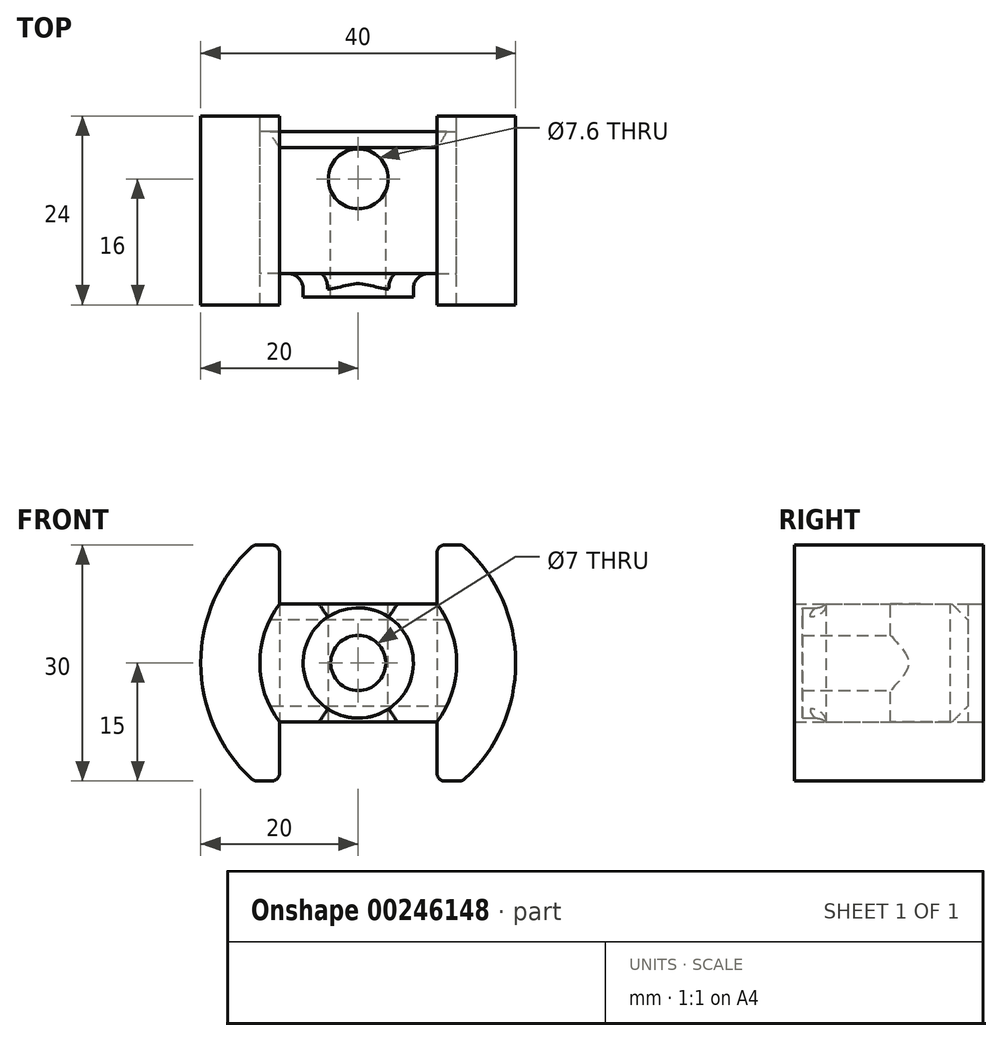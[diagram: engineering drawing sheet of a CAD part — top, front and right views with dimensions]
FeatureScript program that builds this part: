
annotation { "Feature Type Name" : "Feature", "Feature Type Description" : "" }
export const myFeature = defineFeature(function(context is Context, id is Id, definition is map)
    precondition{}
    {
        {
            var Q0;
            Q0=qCreatedBy(makeId("Front.planeOp"),FACE);
            var sketch = newSketch(context, id + "F0", { "sketchPlane" : qUnion([Q0])});
            skArc(sketch, "E0", {"start": v(-13.23, 15) * mm, "mid": v(-20, 0) * mm, "end": v(-13.23, -15) * mm});
            skArc(sketch, "E1", {"start": v(-10, 7.5) * mm, "mid": v(-12.5, 0) * mm, "end": v(-10, -7.5) * mm});
            skLineSegment(sketch, "E2.bottom", {"start": v(-13.23, 15) * mm, "end": v(-10, 15) * mm});
            skLineSegment(sketch, "E2.top", {"start": v(-13.23, -15) * mm, "end": v(-10, -15) * mm});
            skArc(sketch, "E3.trimOffspring", {"start": v(13.23, -15) * mm, "mid": v(20, 0) * mm, "end": v(13.23, 15) * mm});
            skLineSegment(sketch, "E4.bottom", {"start": v(10, 7.5) * mm, "end": v(-10, 7.5) * mm});
            skLineSegment(sketch, "E4.top", {"start": v(10, -7.5) * mm, "end": v(-10, -7.5) * mm});
            skLineSegment(sketch, "E4.left", {"start": v(10, 7.5) * mm, "end": v(10, -7.5) * mm});
            skLineSegment(sketch, "E4.right", {"start": v(-10, 7.5) * mm, "end": v(-10, -7.5) * mm});
            skLineSegment(sketch, "E5", {"start": v(-10, 7.5) * mm, "end": v(-10, 15) * mm});
            skLineSegment(sketch, "E6", {"start": v(10, 7.5) * mm, "end": v(10, 15) * mm});
            skLineSegment(sketch, "E7", {"start": v(10, -7.5) * mm, "end": v(10, -15) * mm});
            skLineSegment(sketch, "E8", {"start": v(-10, -7.5) * mm, "end": v(-10, -15) * mm});
            skLineSegment(sketch, "E9.trimOffspring", {"start": v(10, -15) * mm, "end": v(13.23, -15) * mm});
            skLineSegment(sketch, "E10.trimOffspring", {"start": v(10, 15) * mm, "end": v(13.23, 15) * mm});
            skArc(sketch, "E11.trimOffspring", {"start": v(10, -7.5) * mm, "mid": v(12.5, 0) * mm, "end": v(10, 7.5) * mm});
            skCircle(sketch, "E12", {"center": v(0, 0) * mm, "radius": 7 * mm});
            skCircle(sketch, "E13", {"center": v(0, 0) * mm, "radius": 3.5 * mm});
            skSolve(sketch);
        }
        {
            var Q0;
            Q0=makeQuery(id+"F0.imprint","IMPRINT",FACE,{"disambiguationData":[TD([[makeQuery(id+"F0.imprint","IMPRINT",EDGE,{"derivedFrom":sQuery(id+"F0.wireOp",EDGE,"E0")}),1.0]])]});
            var Q1;
            Q1=makeQuery(id+"F0.imprint","IMPRINT",FACE,{"disambiguationData":[TD([[makeQuery(id+"F0.imprint","IMPRINT",EDGE,{"derivedFrom":sQuery(id+"F0.wireOp",EDGE,"E3.trimOffspring")}),1.0]])]});
            extrude(context, id + "F1", {"entities" : qUnion([Q0, Q1]), "depth" : 24 * mm});
        }
        {
            var Q0;
            Q0=makeQuery(id+"F0.imprint","IMPRINT",FACE,{"disambiguationData":[TD([[makeQuery(id+"F0.imprint","IMPRINT",EDGE,{"derivedFrom":sQuery(id+"F0.wireOp",EDGE,"E1")}),1.0]])]});
            var Q1;
            Q1=makeQuery(id+"F0.imprint","IMPRINT",FACE,{"disambiguationData":[TD([[makeQuery(id+"F0.imprint","IMPRINT",EDGE,{"derivedFrom":sQuery(id+"F0.wireOp",EDGE,"E12")}),1.0]])]});
            var Q2;
            Q2=makeQuery(id+"F0.imprint","IMPRINT",FACE,{"disambiguationData":[TD([[makeQuery(id+"F0.imprint","IMPRINT",EDGE,{"derivedFrom":sQuery(id+"F0.wireOp",EDGE,"E4.bottom")}),1.0]])]});
            var Q3;
            Q3=makeQuery(id+"F0.imprint","IMPRINT",FACE,{"disambiguationData":[TD([[makeQuery(id+"F0.imprint","IMPRINT",EDGE,{"derivedFrom":sQuery(id+"F0.wireOp",EDGE,"E4.left")}),1.0]])]});
            extrude(context, id + "F2", {"entities" : qUnion([Q0, Q1, Q2, Q3]), "depth" : 20 * mm, "hasSecondDirection" : true, "secondDirectionOppositeDirection" : false, "secondDirectionDepth" : 2 * mm});
        }
        {
            var Q0;
            Q0=makeQuery(id+"F0.imprint","IMPRINT",FACE,{"disambiguationData":[TD([[makeQuery(id+"F0.imprint","IMPRINT",EDGE,{"derivedFrom":sQuery(id+"F0.wireOp",EDGE,"E12")}),1.0]])]});
            var Q1;
            Q1=makeQuery(id+"F0.imprint","IMPRINT",FACE,{"disambiguationData":[TD([[makeQuery(id+"F0.imprint","IMPRINT",EDGE,{"derivedFrom":sQuery(id+"F0.wireOp",EDGE,"E13")}),1.0]])]});
            extrude(context, id + "F3", {"entities" : qUnion([Q0, Q1]), "operationType" : NewBodyOperationType.ADD, "depth" : 23 * mm, "hasSecondDirection" : true, "secondDirectionOppositeDirection" : false, "secondDirectionDepth" : 2 * mm});
        }
        {
            var Q0;
            Q0=makeQuery(id+"F2.opExtrude","SWEPT_FACE",FACE,{"disambiguationData":[OSD([sQuery(id+"F0.wireOp",EDGE,"E4.top")])]});
            var sketch = newSketch(context, id + "F4", { "sketchPlane" : qUnion([Q0])});
            skLineSegment(sketch, "E14", {"start": v(0, 0) * mm, "end": v(0, 8) * mm});
            skCircle(sketch, "E15", {"center": v(0, 8) * mm, "radius": 3.8 * mm});
            skSolve(sketch);
        }
        {
            var Q0;
            Q0=sQuery(id+"F4.wireOp",VERTEX,"E15.center");
            var Q1;
            Q1=makeQuery(id+"F2.opExtrude","SWEPT_BODY",BODY,{"disambiguationData":[OSD([sQuery(id+"F0.wireOp",EDGE,"E1"),sQuery(id+"F0.wireOp",EDGE,"E4.bottom"),sQuery(id+"F0.wireOp",EDGE,"E4.top"),sQuery(id+"F0.wireOp",EDGE,"E11.trimOffspring"),sQuery(id+"F0.wireOp",EDGE,"E13")])]});
            hole(context, id + "F5", {"style" : HoleStyle.SIMPLE, "endStyle" : HoleEndStyle.BLIND, "holeDiameter" : 7.6 * mm, "holeDepth" : 17 * mm, "tappedDepth" : 12.7 * mm, "tapClearance" : 3, "locations" : qUnion([Q0]), "scope" : qUnion([Q1]), "startStyle" : HoleStartStyle.PART});
        }
        {
            var Q0;
            Q0=makeQuery(id+"F3.opExtrude","CAP_FACE",FACE,{"disambiguationData":[OSD([sQuery(id+"F0.wireOp",EDGE,"E12")])],"isStart":false});
            var sketch = newSketch(context, id + "F6", { "sketchPlane" : qUnion([Q0])});
            skCircle(sketch, "E16", {"center": v(0, 0) * mm, "radius": 3.5 * mm});
            skSolve(sketch);
        }
        {
            var Q0;
            Q0=sQuery(id+"F6.wireOp",VERTEX,"E16.center");
            var Q1;
            Q1=makeQuery(id+"F2.opExtrude","SWEPT_BODY",BODY,{"disambiguationData":[OSD([sQuery(id+"F0.wireOp",EDGE,"E1"),sQuery(id+"F0.wireOp",EDGE,"E4.bottom"),sQuery(id+"F0.wireOp",EDGE,"E4.top"),sQuery(id+"F0.wireOp",EDGE,"E11.trimOffspring"),sQuery(id+"F0.wireOp",EDGE,"E13")])]});
            hole(context, id + "F7", {"style" : HoleStyle.SIMPLE, "endStyle" : HoleEndStyle.BLIND, "holeDiameter" : 7 * mm, "holeDepth" : 15 * mm, "tappedDepth" : 12.7 * mm, "tapClearance" : 3, "locations" : qUnion([Q0]), "scope" : qUnion([Q1]), "startStyle" : HoleStartStyle.PART});
        }
        {
            var Q0;
            Q0=makeQuery(id+"F1.opExtrude","SWEPT_EDGE",EDGE,{"disambiguationData":[OSD([sQuery(id+"F0.wireOp",EDGE,"E2.bottom"),sQuery(id+"F0.wireOp",EDGE,"E5")])]});
            var Q1;
            Q1=makeQuery(id+"F1.opExtrude","SWEPT_EDGE",EDGE,{"disambiguationData":[OSD([sQuery(id+"F0.wireOp",EDGE,"E0"),sQuery(id+"F0.wireOp",EDGE,"E2.bottom")])]});
            var Q2;
            Q2=makeQuery(id+"F1.opExtrude","SWEPT_EDGE",EDGE,{"disambiguationData":[OSD([sQuery(id+"F0.wireOp",EDGE,"E2.top"),sQuery(id+"F0.wireOp",EDGE,"E8")])]});
            var Q3;
            Q3=makeQuery(id+"F1.opExtrude","SWEPT_EDGE",EDGE,{"disambiguationData":[OSD([sQuery(id+"F0.wireOp",EDGE,"E0"),sQuery(id+"F0.wireOp",EDGE,"E2.top")])]});
            var Q4;
            Q4=makeQuery(id+"F1.opExtrude","SWEPT_EDGE",EDGE,{"disambiguationData":[OSD([sQuery(id+"F0.wireOp",EDGE,"E3.trimOffspring"),sQuery(id+"F0.wireOp",EDGE,"E10.trimOffspring")])]});
            var Q5;
            Q5=makeQuery(id+"F1.opExtrude","SWEPT_EDGE",EDGE,{"disambiguationData":[OSD([sQuery(id+"F0.wireOp",EDGE,"E6"),sQuery(id+"F0.wireOp",EDGE,"E10.trimOffspring")])]});
            var Q6;
            Q6=makeQuery(id+"F1.opExtrude","SWEPT_EDGE",EDGE,{"disambiguationData":[OSD([sQuery(id+"F0.wireOp",EDGE,"E7"),sQuery(id+"F0.wireOp",EDGE,"E9.trimOffspring")])]});
            var Q7;
            Q7=makeQuery(id+"F1.opExtrude","SWEPT_EDGE",EDGE,{"disambiguationData":[OSD([sQuery(id+"F0.wireOp",EDGE,"E3.trimOffspring"),sQuery(id+"F0.wireOp",EDGE,"E9.trimOffspring")])]});
            fillet(context, id + "F8", {"entities" : qUnion([Q0, Q1, Q2, Q3, Q4, Q5, Q6, Q7]), "radius" : 1 * mm, "tangentPropagation" : true, "allowEdgeOverflow" : false});
        }
        {
            var Q0;
            Q0=makeQuery(id+"F0.imprint","IMPRINT",FACE,{"disambiguationData":[TD([[makeQuery(id+"F0.imprint","IMPRINT",EDGE,{"derivedFrom":sQuery(id+"F0.wireOp",EDGE,"E1")}),1.0]])]});
            var Q1;
            Q1=makeQuery(id+"F0.imprint","IMPRINT",FACE,{"disambiguationData":[TD([[makeQuery(id+"F0.imprint","IMPRINT",EDGE,{"derivedFrom":sQuery(id+"F0.wireOp",EDGE,"E4.left")}),1.0]])]});
            extrude(context, id + "F9", {"entities" : qUnion([Q0, Q1]), "depth" : 2 * mm});
        }
        {
            var Q0;
            Q0=makeQuery(id+"F2.opExtrude","CAP_EDGE",EDGE,{"disambiguationData":[OSD([sQuery(id+"F0.wireOp",EDGE,"E4.top")])],"isStart":true});
            var Q1;
            Q1=makeQuery(id+"F2.opExtrude","CAP_EDGE",EDGE,{"disambiguationData":[OSD([sQuery(id+"F0.wireOp",EDGE,"E4.bottom")])],"isStart":true});
            chamfer(context, id + "F10", {"entities" : qUnion([Q0, Q1]), "width" : 2 * mm, "tangentPropagation" : true});
        }
        {
            var Q0;
            Q0=makeQuery(id+"F3.boolean.opBoolean","INTERSECT",EDGE,{"derivedFrom":[makeQuery(id+"F2.opExtrude","CAP_FACE",FACE,{"disambiguationData":[OSD([sQuery(id+"F0.wireOp",EDGE,"E1"),sQuery(id+"F0.wireOp",EDGE,"E4.bottom"),sQuery(id+"F0.wireOp",EDGE,"E4.top"),sQuery(id+"F0.wireOp",EDGE,"E11.trimOffspring"),sQuery(id+"F0.wireOp",EDGE,"E13")])],"isStart":false}),makeQuery(id+"F3.opExtrude","SWEPT_FACE",FACE,{"disambiguationData":[OSD([sQuery(id+"F0.wireOp",EDGE,"E12")])]})]});
            fillet(context, id + "F11", {"entities" : qUnion([Q0]), "radius" : 2 * mm, "tangentPropagation" : true, "allowEdgeOverflow" : false});
        }
    });
